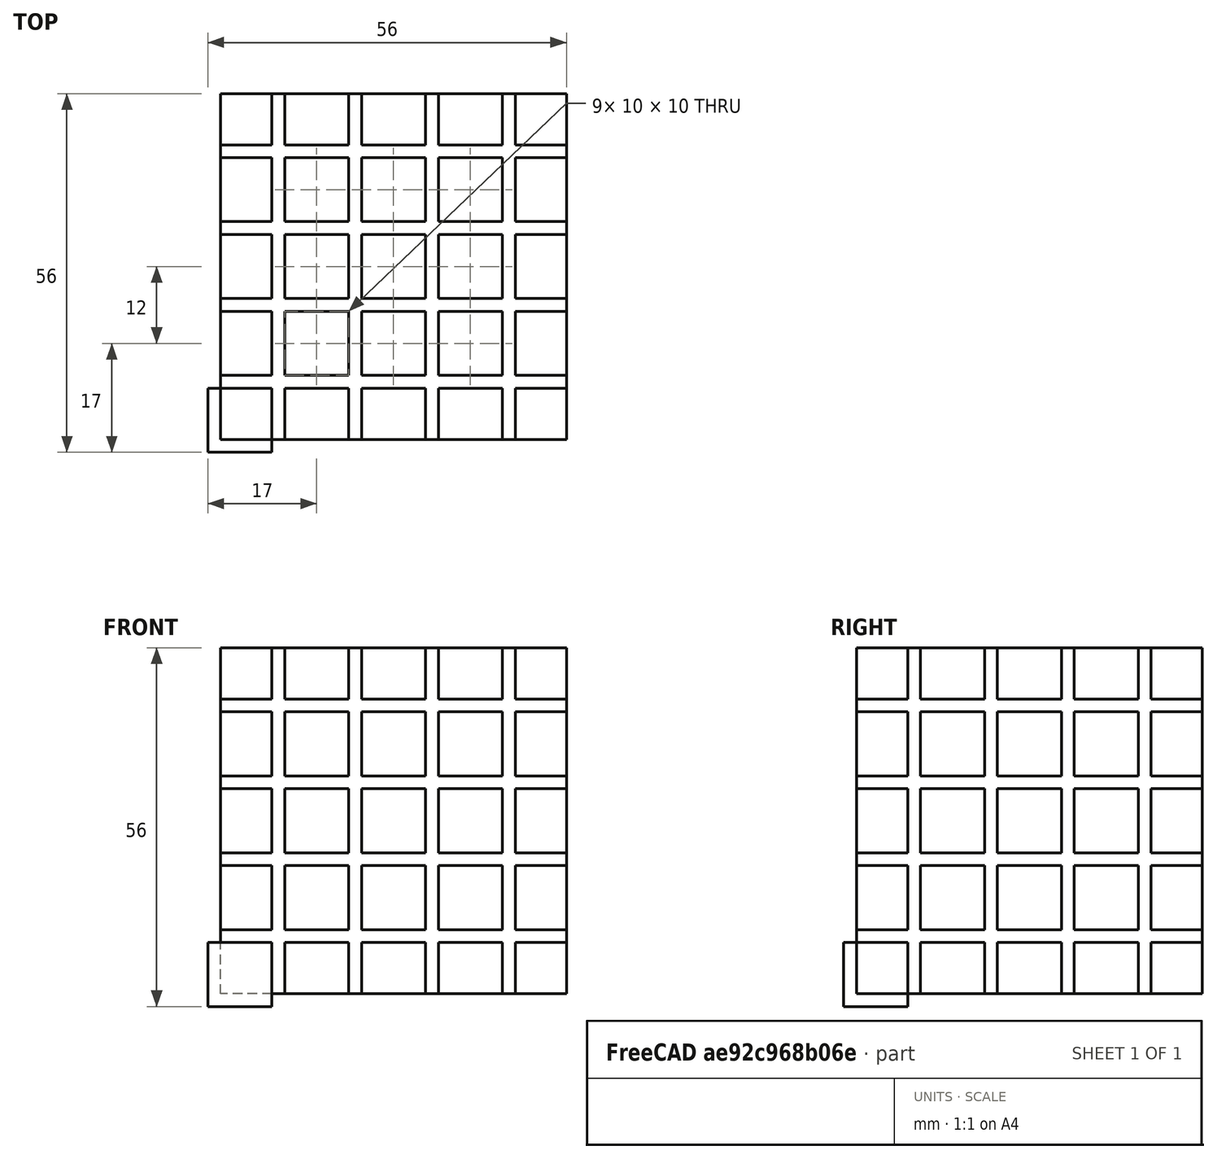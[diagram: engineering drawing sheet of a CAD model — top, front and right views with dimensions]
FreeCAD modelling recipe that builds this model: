
FCSTD DOCUMENT  (FreeCAD 0.21R33694 (Git))
Label: OJT1_T10P03_gofre3D
License: All rights reserved
LicenseURL: http://en.wikipedia.org/wiki/All_rights_reserved
objects: Part::Box×2, Part::FeaturePython×1, Part::Cut×1
note: 3 computed .brp shape members not serialized (recipe doc carries the construction recipe); baked Part::Feature solids carry a one-line shape summary decoded from their .brp

FEATURE [Part::Box] Box  label="Cube"
  AttacherType = Attacher::AttachEngine3D
  Height = 10
  Length = 10
  Width = 10
FEATURE [Part::Box] Box001  label="Cube001"
  AttacherType = Attacher::AttachEngine3D
  Height = 54
  Length = 54
  Placement = pos=(2,2,2) rot=(0,0,1;0rad)
  Width = 54
FEATURE [Part::FeaturePython] Array  # Draft array (typed FeaturePython)
  AlwaysSyncPlacement = false
  Angle = 360
  ArrayType = 0
  Axis = (0,0,1)
  Base = -> Box
  Center = (0,0,0)
  Count = 125
  ExpandArray = false
  Fuse = false
  IntervalAxis = (0,0,0)
  IntervalX = (12,0,0)
  IntervalY = (0,12,0)
  IntervalZ = (0,0,12)
  NumberCircles = 3
  NumberPolar = 5
  NumberX = 5
  NumberY = 5
  NumberZ = 5
  PlacementList = 125 placements: [(0,0,0),(0,0,12),(0,0,24),(0,0,36),(0,0,48),(0,12,0),(0,12,12),(0,12,24),(0,12,36),(0,12,48),(0,24,0),(0,24,12),(0,24,24),(0,24,36),(0,24,48),(0,36,0),(0,36,12),(0,36,24),(0,36,36),(0,36,48),(0,48,0),(0,48,12),(0,48,24),(0,48,36),(0,48,48),(12,0,0),(12,0,12),(12,0,24),(12,0,36),(12,0,48),(12,12,0),(12,12,12),(12,12,24),(12,12,36),(12,12,48),(12,24,0),(12,24,12),(12,24,24),(12,24,36),(12,24,48),+85 more]
  RadialDistance = 50
  ScaleList = (125) [(1,1,1),(1,1,1),(1,1,1),(1,1,1),(1,1,1),(1,1,1),(1,1,1),(1,1,1),(1,1,1),(1,1,1),(1,1,1),(1,1,1),(1,1,1),(1,1,1),(1,1,1),(1,1,1),(1,1,1),(1,1,1),+107 more]
  Symmetry = 1
  TangentialDistance = 25
FEATURE [Part::Cut] Cut
  Base = -> Box001
  Refine = true
  Tool = -> Array
